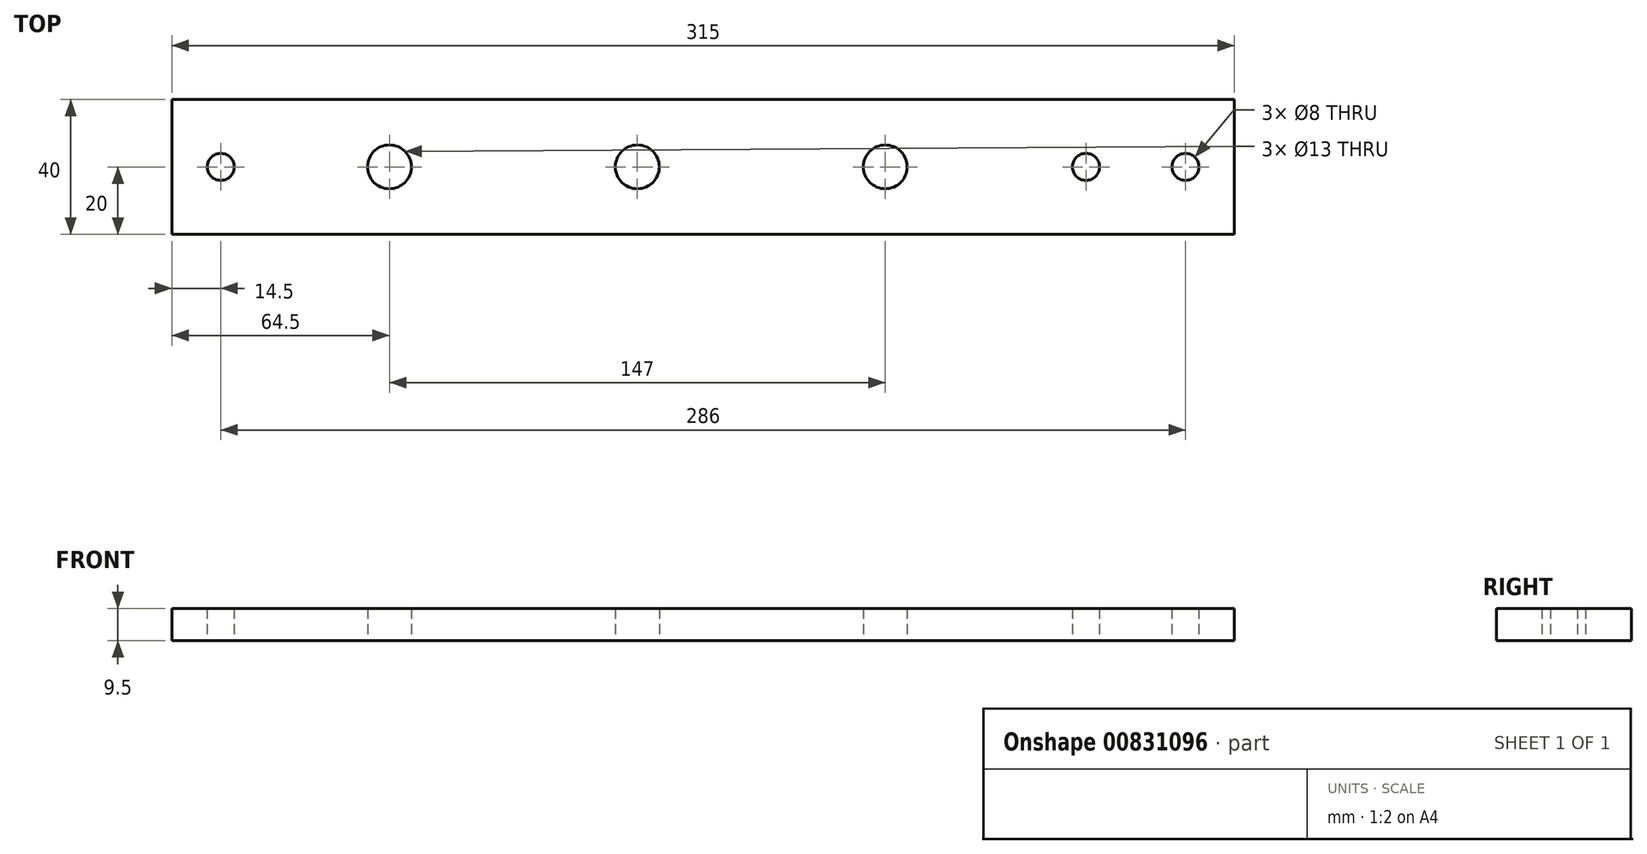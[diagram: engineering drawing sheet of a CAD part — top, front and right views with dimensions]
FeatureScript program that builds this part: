
annotation { "Feature Type Name" : "Feature", "Feature Type Description" : "" }
export const myFeature = defineFeature(function(context is Context, id is Id, definition is map)
    precondition{}
    {
        {
            var Q0;
            Q0=qCreatedBy(makeId("Top.planeOp"),FACE);
            var sketch = newSketch(context, id + "F0", { "sketchPlane" : qUnion([Q0])});
            skLineSegment(sketch, "E0.bottom", {"start": v(0, 0) * mm, "end": v(315, 0) * mm});
            skLineSegment(sketch, "E0.top", {"start": v(0, 40) * mm, "end": v(315, 40) * mm});
            skLineSegment(sketch, "E0.left", {"start": v(0, 0) * mm, "end": v(0, 40) * mm});
            skLineSegment(sketch, "E0.right", {"start": v(315, 0) * mm, "end": v(315, 40) * mm});
            skCircle(sketch, "E1", {"center": v(138, 20) * mm, "radius": 6.5 * mm});
            skPoint(sketch, "E1.centerSnap0", {"position": v(0, 20) * mm});
            skCircle(sketch, "E2", {"center": v(211.5, 20) * mm, "radius": 6.5 * mm});
            skCircle(sketch, "E3", {"center": v(14.5, 20) * mm, "radius": 4 * mm});
            skCircle(sketch, "E4", {"center": v(64.5, 20) * mm, "radius": 6.5 * mm});
            skCircle(sketch, "E5", {"center": v(271, 20) * mm, "radius": 4 * mm});
            skCircle(sketch, "E6", {"center": v(300.5, 20) * mm, "radius": 4 * mm});
            skPoint(sketch, "E6.centerSnap0", {"position": v(315, 20) * mm});
            skSolve(sketch);
        }
        {
            var Q0;
            Q0 = qSketchRegion(id + "F0", true);
            extrude(context, id + "F1", {"entities" : qUnion([Q0]), "depth" : 9.5 * mm, "offsetDistance" : 25 * mm});
        }
    });
